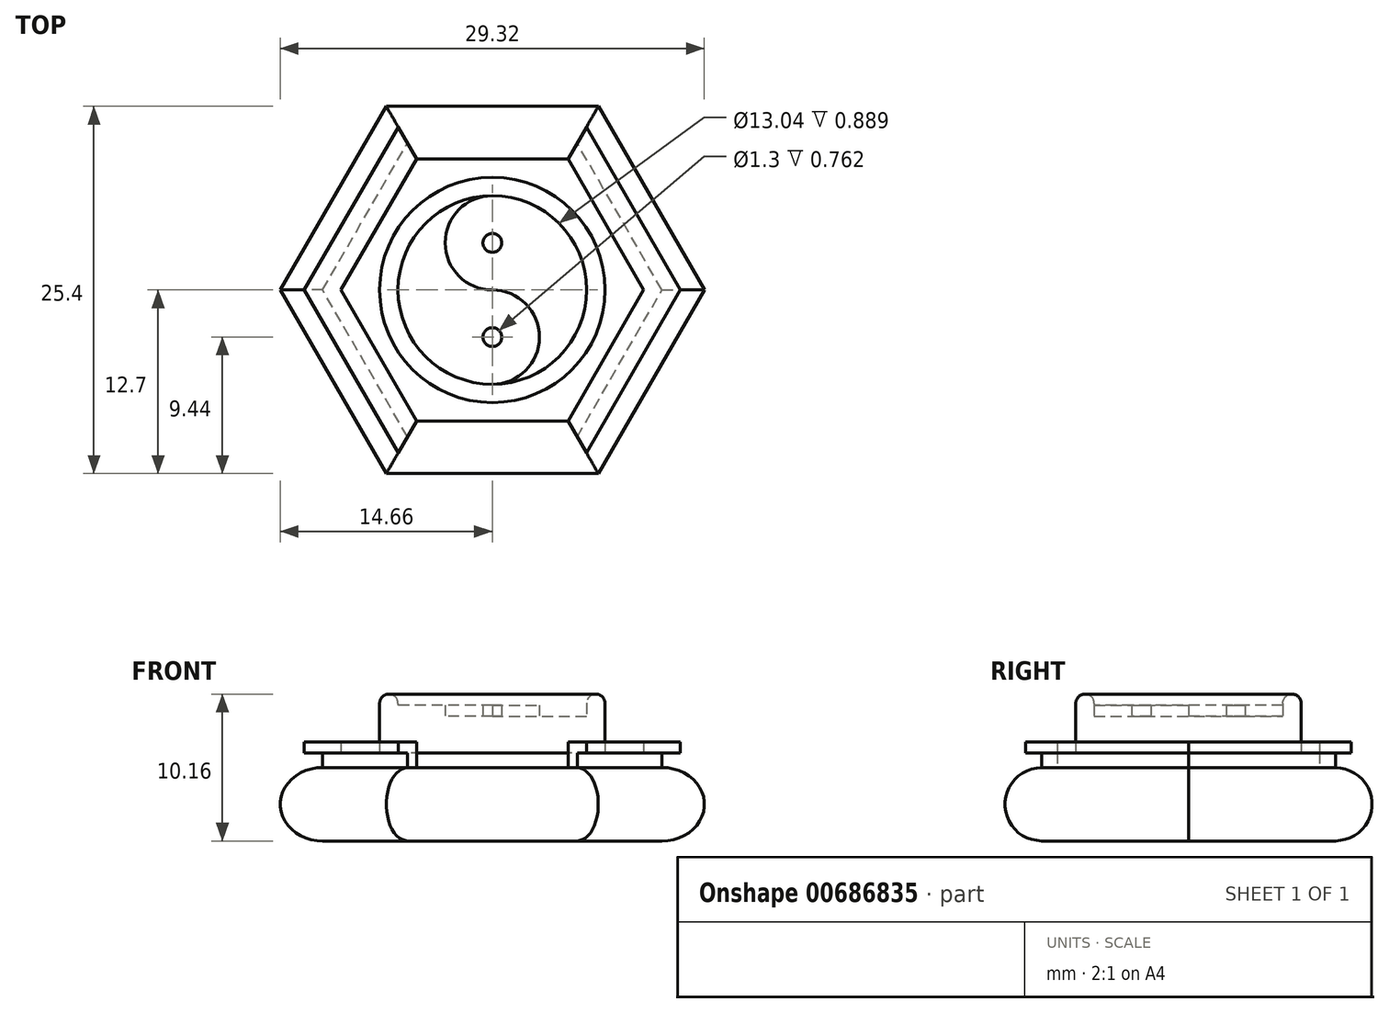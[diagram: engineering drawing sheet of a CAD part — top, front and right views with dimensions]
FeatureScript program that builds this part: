
annotation { "Feature Type Name" : "Feature", "Feature Type Description" : "" }
export const myFeature = defineFeature(function(context is Context, id is Id, definition is map)
    precondition{}
    {
        {
            var Q0;
            Q0=qCreatedBy(makeId("Front.planeOp"),FACE);
            var sketch = newSketch(context, id + "F0", { "sketchPlane" : qUnion([Q0])});
            skLineSegment(sketch, "E0", {"start": v(0, 0) * mm, "end": v(-12.7, 0) * mm});
            skLineSegment(sketch, "E1", {"start": v(-12.7, 0) * mm, "end": v(-12.7, 5.08) * mm, "construction": true});
            skLineSegment(sketch, "E2", {"start": v(12.7, 5.08) * mm, "end": v(12.7, 0) * mm, "construction": true});
            skLineSegment(sketch, "E3", {"start": v(12.7, 0) * mm, "end": v(0, 0) * mm});
            skArc(sketch, "E4", {"start": v(12.7, 0) * mm, "mid": v(15.24, 2.54) * mm, "end": v(12.7, 5.08) * mm});
            skArc(sketch, "E5", {"start": v(-12.7, 5.08) * mm, "mid": v(-15.24, 2.54) * mm, "end": v(-12.7, 0) * mm});
            skLineSegment(sketch, "E6", {"start": v(0, 0) * mm, "end": v(0, 5.08) * mm, "construction": true});
            skLineSegment(sketch, "E7", {"start": v(12.7, 2.54) * mm, "end": v(15.24, 2.54) * mm, "construction": true});
            skLineSegment(sketch, "E8", {"start": v(-12.7, 5.08) * mm, "end": v(12.7, 5.08) * mm});
            skPoint(sketch, "E9", {"position": v(0, 5.08) * mm});
            skSolve(sketch);
        }
        {
            var Q0;
            Q0=qSketchRegion(id+"F0",true);
            extrude(context, id + "F1", {"entities" : qUnion([Q0]), "endBound" : BoundingType.SYMMETRIC, "depth" : 25.4 * mm, "offsetDistance" : 25.4 * mm});
        }
        {
            var Q0;
            Q0=qCreatedBy(makeId("Right.planeOp"),FACE);
            var sketch = newSketch(context, id + "F2", { "sketchPlane" : qUnion([Q0])});
            skLineSegment(sketch, "E10", {"start": v(0, 0) * mm, "end": v(-10.16, 0) * mm, "construction": true});
            skLineSegment(sketch, "E11", {"start": v(0, 0) * mm, "end": v(10.16, 0) * mm, "construction": true});
            skLineSegment(sketch, "E12", {"start": v(-10.16, 0) * mm, "end": v(-10.16, 5.08) * mm, "construction": true});
            skLineSegment(sketch, "E13", {"start": v(10.16, 0) * mm, "end": v(10.16, 5.08) * mm, "construction": true});
            skArc(sketch, "E14", {"start": v(10.16, 0) * mm, "mid": v(12.7, 2.54) * mm, "end": v(10.16, 5.08) * mm});
            skArc(sketch, "E15", {"start": v(-10.16, 5.08) * mm, "mid": v(-12.7, 2.54) * mm, "end": v(-10.16, 0) * mm});
            skLineSegment(sketch, "E16", {"start": v(0, 0) * mm, "end": v(0, 5.08) * mm, "construction": true});
            skLineSegment(sketch, "E17", {"start": v(29.21, 5.08) * mm, "end": v(29.21, 0) * mm});
            skLineSegment(sketch, "E18", {"start": v(-29.21, 5.08) * mm, "end": v(-29.21, 0) * mm});
            skLineSegment(sketch, "E19", {"start": v(-10.16, 0) * mm, "end": v(-29.21, 0) * mm});
            skLineSegment(sketch, "E20", {"start": v(-10.16, 2.54) * mm, "end": v(-12.7, 2.54) * mm, "construction": true});
            skLineSegment(sketch, "E21", {"start": v(29.21, 0) * mm, "end": v(10.16, 0) * mm});
            skLineSegment(sketch, "E22", {"start": v(0, 0) * mm, "end": v(0, 0) * mm});
            skLineSegment(sketch, "E23", {"start": v(10.16, 5.08) * mm, "end": v(-10.16, 5.08) * mm, "construction": true});
            skLineSegment(sketch, "E24", {"start": v(29.21, 5.08) * mm, "end": v(10.16, 5.08) * mm});
            skLineSegment(sketch, "E25", {"start": v(-29.21, 5.08) * mm, "end": v(-10.16, 5.08) * mm});
            skSolve(sketch);
        }
        {
            var Q0;
            Q0=qSketchRegion(id+"F2",true);
            extrude(context, id + "F3", {"entities" : qUnion([Q0]), "operationType" : NewBodyOperationType.REMOVE, "endBound" : BoundingType.SYMMETRIC, "depth" : 50.8 * mm, "offsetDistance" : 25.4 * mm});
        }
        {
            var Q0;
            Q0=sQuery(id+"F0.wireOp",EDGE,"E6");
            cPlane(context, id + "F4", {"entities" : qUnion([Q0]), "cplaneType" : CPlaneType.LINE_ANGLE, "offset" : 25.4 * mm, "angle" : 120 * degree, "width" : 152.4 * mm, "height" : 152.4 * mm});
        }
        {
            var Q0;
            Q0=qCreatedBy(id+"F4.planeOp",FACE);
            var sketch = newSketch(context, id + "F5", { "sketchPlane" : qUnion([Q0])});
            skLineSegment(sketch, "E26", {"start": v(0, 0) * mm, "end": v(-10.16, 0) * mm, "construction": true});
            skLineSegment(sketch, "E27", {"start": v(0, 0) * mm, "end": v(10.16, 0) * mm, "construction": true});
            skLineSegment(sketch, "E28", {"start": v(-10.16, 0) * mm, "end": v(-10.16, 5.08) * mm, "construction": true});
            skLineSegment(sketch, "E29", {"start": v(10.16, 0) * mm, "end": v(10.16, 5.08) * mm, "construction": true});
            skArc(sketch, "E30", {"start": v(10.16, 0) * mm, "mid": v(12.7, 2.54) * mm, "end": v(10.16, 5.08) * mm});
            skArc(sketch, "E31", {"start": v(-10.16, 5.08) * mm, "mid": v(-12.7, 2.54) * mm, "end": v(-10.16, 0) * mm});
            skLineSegment(sketch, "E32", {"start": v(0, 0) * mm, "end": v(0, 5.08) * mm, "construction": true});
            skLineSegment(sketch, "E33", {"start": v(29.21, 5.08) * mm, "end": v(29.21, 0) * mm});
            skLineSegment(sketch, "E34", {"start": v(-29.21, 5.08) * mm, "end": v(-29.21, 0) * mm});
            skLineSegment(sketch, "E35", {"start": v(-10.16, 0) * mm, "end": v(-29.21, 0) * mm});
            skLineSegment(sketch, "E36", {"start": v(-10.16, 2.54) * mm, "end": v(-12.7, 2.54) * mm, "construction": true});
            skLineSegment(sketch, "E37", {"start": v(29.21, 0) * mm, "end": v(10.16, 0) * mm});
            skLineSegment(sketch, "E38", {"start": v(0, 0) * mm, "end": v(0, 0) * mm});
            skLineSegment(sketch, "E39", {"start": v(10.16, 5.08) * mm, "end": v(-10.16, 5.08) * mm, "construction": true});
            skLineSegment(sketch, "E40", {"start": v(29.21, 5.08) * mm, "end": v(10.16, 5.08) * mm});
            skLineSegment(sketch, "E41", {"start": v(-29.21, 5.08) * mm, "end": v(-10.16, 5.08) * mm});
            skSolve(sketch);
        }
        {
            var Q0;
            Q0=qSketchRegion(id+"F5",true);
            var Q1;
            Q1=sQuery(id+"FHUch5MhYWofbFd_1.wireOp",EDGE,"UJUXWhbe-ns99-R938-MBjs-qnEI7qI75ZtX");
            var Q2;
            Q2=sQuery(id+"FHUch5MhYWofbFd_1.wireOp",EDGE,"TGRI2bbO-5mKc-ZYGL-RI2u-ax8UZepCr2S6");
            var Q3;
            Q3=sQuery(id+"FHUch5MhYWofbFd_1.wireOp",EDGE,"3EN97P5a-7fpQ-fkxS-kFIG-O94JdEreBvdc");
            var Q4;
            Q4=sQuery(id+"FHUch5MhYWofbFd_1.wireOp",EDGE,"BLXI86f6-p3FV-xg8e-vcjV-MuaEN1ZbEeBN");
            var Q5;
            Q5=sQuery(id+"FHUch5MhYWofbFd_1.wireOp",EDGE,"K6Pg9hkI-HhUm-eWt8-lgsy-rQcUfMNRkeRX");
            var Q6;
            Q6=sQuery(id+"FHUch5MhYWofbFd_1.wireOp",EDGE,"8MWXePed-qfWZ-9kiI-xQLn-RgFZeWpe4DeW");
            var Q7;
            Q7=sQuery(id+"FHUch5MhYWofbFd_1.wireOp",EDGE,"ujHeR1Bt-oqxH-zWrO-aF7a-1cGxx1oxEC4p");
            var Q8;
            Q8=sQuery(id+"FHUch5MhYWofbFd_1.wireOp",EDGE,"ezDig2bh-fpcZ-qdXg-hfEw-k3bdO8GFTHoY");
            var Q9;
            Q9=sQuery(id+"FHUch5MhYWofbFd_1.wireOp",EDGE,"TL3t9Hpy-tibO-WM6d-k033-ZjCVjvvUcohB");
            var Q10;
            Q10=sQuery(id+"FHUch5MhYWofbFd_1.wireOp",EDGE,"H6XLH3zd-cpDk-JRaX-qujs-Kg6a5HbhHDUq");
            var Q11;
            Q11=sQuery(id+"FHUch5MhYWofbFd_1.wireOp",EDGE,"XlrNxneH-uq2I-L97s-EfPg-StDvBexp0ezL");
            var Q12;
            Q12=sQuery(id+"FHUch5MhYWofbFd_1.wireOp",EDGE,"V9PWrxtB-5fyD-G3Op-kF2t-xwj5HEO20ic1");
            var Q13;
            Q13=sQuery(id+"FHUch5MhYWofbFd_1.wireOp",EDGE,"DBsLzJAx-6rkW-YoXi-OfuC-MLqgEexGkzpa");
            extrude(context, id + "F6", {"entities" : qUnion([Q0]), "operationType" : NewBodyOperationType.REMOVE, "surfaceEntities" : qUnion([Q1, Q2, Q3, Q4, Q5, Q6, Q7, Q8, Q9, Q10, Q11, Q12, Q13]), "endBound" : BoundingType.SYMMETRIC, "oppositeDirection" : true, "depth" : 50.8 * mm, "offsetDistance" : 25.4 * mm});
        }
        {
            var Q0;
            Q0=sQuery(id+"F0.wireOp",EDGE,"E6");
            cPlane(context, id + "F7", {"entities" : qUnion([Q0]), "cplaneType" : CPlaneType.LINE_ANGLE, "offset" : 25.4 * mm, "angle" : 60 * degree, "width" : 152.4 * mm, "height" : 152.4 * mm});
        }
        {
            var Q0;
            Q0=qCreatedBy(id+"F7.planeOp",FACE);
            var sketch = newSketch(context, id + "F8", { "sketchPlane" : qUnion([Q0])});
            skLineSegment(sketch, "E42", {"start": v(0, 0) * mm, "end": v(-10.16, 0) * mm, "construction": true});
            skLineSegment(sketch, "E43", {"start": v(0, 0) * mm, "end": v(10.16, 0) * mm, "construction": true});
            skLineSegment(sketch, "E44", {"start": v(-10.16, 0) * mm, "end": v(-10.16, 5.08) * mm, "construction": true});
            skLineSegment(sketch, "E45", {"start": v(10.16, 0) * mm, "end": v(10.16, 5.08) * mm, "construction": true});
            skArc(sketch, "E46", {"start": v(10.16, 0) * mm, "mid": v(12.7, 2.54) * mm, "end": v(10.16, 5.08) * mm});
            skArc(sketch, "E47", {"start": v(-10.16, 5.08) * mm, "mid": v(-12.7, 2.54) * mm, "end": v(-10.16, 0) * mm});
            skLineSegment(sketch, "E48", {"start": v(0, 0) * mm, "end": v(0, 5.08) * mm, "construction": true});
            skLineSegment(sketch, "E49", {"start": v(29.21, 5.08) * mm, "end": v(29.21, 0) * mm});
            skLineSegment(sketch, "E50", {"start": v(-29.21, 5.08) * mm, "end": v(-29.21, 0) * mm});
            skLineSegment(sketch, "E51", {"start": v(-10.16, 0) * mm, "end": v(-29.21, 0) * mm});
            skLineSegment(sketch, "E52", {"start": v(-10.16, 2.54) * mm, "end": v(-12.7, 2.54) * mm, "construction": true});
            skLineSegment(sketch, "E53", {"start": v(29.21, 0) * mm, "end": v(10.16, 0) * mm});
            skLineSegment(sketch, "E54", {"start": v(0, 0) * mm, "end": v(0, 0) * mm});
            skLineSegment(sketch, "E55", {"start": v(10.16, 5.08) * mm, "end": v(-10.16, 5.08) * mm, "construction": true});
            skLineSegment(sketch, "E56", {"start": v(29.21, 5.08) * mm, "end": v(10.16, 5.08) * mm});
            skLineSegment(sketch, "E57", {"start": v(-29.21, 5.08) * mm, "end": v(-10.16, 5.08) * mm});
            skSolve(sketch);
        }
        {
            var Q0;
            Q0=qSketchRegion(id+"F8",true);
            extrude(context, id + "F9", {"entities" : qUnion([Q0]), "operationType" : NewBodyOperationType.REMOVE, "endBound" : BoundingType.SYMMETRIC, "oppositeDirection" : true, "depth" : 50.8 * mm, "offsetDistance" : 25.4 * mm});
        }
        {
            var Q0;
            Q0=makeQuery(id+"FriaykctB5W3C7Q_1.boolean.opBoolean","SPLIT",FACE,{"disambiguationData":[TD([makeQuery(id+"F6.boolean.opBoolean","COPY",FACE,{"derivedFrom":makeQuery(id+"F6.opExtrude","SWEPT_FACE",FACE,{"disambiguationData":[OSD([sQuery(id+"F5.wireOp",EDGE,"E30")])]})})])],"derivedFrom":makeQuery(id+"F1.opExtrude","SWEPT_FACE",FACE,{"disambiguationData":[OSD([sQuery(id+"F0.wireOp",EDGE,"E8")])]})});
            var sketch = newSketch(context, id + "F10", { "sketchPlane" : qUnion([Q0])});
            skLineSegment(sketch, "E58", {"start": v(5.87, 10.16) * mm, "end": v(6.5, 11.26) * mm});
            skLineSegment(sketch, "E59", {"start": v(6.5, 11.26) * mm, "end": v(13, 0) * mm});
            skLineSegment(sketch, "E60", {"start": v(13, 0) * mm, "end": v(6.5, -11.26) * mm});
            skLineSegment(sketch, "E61", {"start": v(-5.87, 10.16) * mm, "end": v(-6.5, 11.26) * mm});
            skLineSegment(sketch, "E62", {"start": v(-6.5, 11.26) * mm, "end": v(-13, 0) * mm});
            skLineSegment(sketch, "E63", {"start": v(-13, 0) * mm, "end": v(-6.5, -11.26) * mm});
            skLineSegment(sketch, "E64", {"start": v(-6.5, -11.26) * mm, "end": v(-5.87, -10.16) * mm});
            skLineSegment(sketch, "E65", {"start": v(6.5, -11.26) * mm, "end": v(5.87, -10.16) * mm});
            skLineSegment(sketch, "E66", {"start": v(5.23, 9.06) * mm, "end": v(10.46, 0) * mm});
            skLineSegment(sketch, "E67", {"start": v(10.46, 0) * mm, "end": v(5.23, -9.06) * mm});
            skLineSegment(sketch, "E68", {"start": v(5.23, -9.06) * mm, "end": v(5.87, -10.16) * mm});
            skLineSegment(sketch, "E69", {"start": v(0, 0) * mm, "end": v(5.23, 9.06) * mm, "construction": true});
            skLineSegment(sketch, "E70", {"start": v(5.23, 9.06) * mm, "end": v(5.87, 10.16) * mm});
            skLineSegment(sketch, "E71", {"start": v(0, 0) * mm, "end": v(-5.23, 9.06) * mm, "construction": true});
            skLineSegment(sketch, "E72", {"start": v(-5.23, 9.06) * mm, "end": v(-5.87, 10.16) * mm});
            skLineSegment(sketch, "E73", {"start": v(-5.23, 9.06) * mm, "end": v(-10.46, 0) * mm});
            skLineSegment(sketch, "E74", {"start": v(-10.46, 0) * mm, "end": v(-5.23, -9.06) * mm});
            skLineSegment(sketch, "E75", {"start": v(-5.23, -9.06) * mm, "end": v(-5.87, -10.16) * mm});
            skLineSegment(sketch, "E76", {"start": v(-5.23, -9.06) * mm, "end": v(5.23, -9.06) * mm});
            skLineSegment(sketch, "E77", {"start": v(-5.23, 9.06) * mm, "end": v(5.23, 9.06) * mm});
            skSolve(sketch);
        }
        {
            var Q0;
            Q0=makeQuery(id+"F10.imprint","IMPRINT",FACE,{"disambiguationData":[TD([[makeQuery(id+"F10.imprint","IMPRINT",EDGE,{"derivedFrom":sQuery(id+"F10.wireOp",EDGE,"E72")}),1.0]])]});
            var Q1;
            Q1=makeQuery(id+"F10.imprint","IMPRINT",FACE,{"disambiguationData":[TD([[makeQuery(id+"F10.imprint","IMPRINT",EDGE,{"derivedFrom":sQuery(id+"F10.wireOp",EDGE,"E61")}),1.0]])]});
            var Q2;
            Q2=makeQuery(id+"F10.imprint","IMPRINT",FACE,{"disambiguationData":[TD([[makeQuery(id+"F10.imprint","IMPRINT",EDGE,{"derivedFrom":sQuery(id+"F10.wireOp",EDGE,"E66")}),1.0]])]});
            var Q3;
            Q3=makeQuery(id+"F10.imprint","IMPRINT",FACE,{"disambiguationData":[TD([[makeQuery(id+"F10.imprint","IMPRINT",EDGE,{"derivedFrom":sQuery(id+"F10.wireOp",EDGE,"E58")}),-1.0]])]});
            extrude(context, id + "F11", {"entities" : qUnion([Q0, Q1, Q2, Q3]), "operationType" : NewBodyOperationType.ADD, "depth" : 1.78 * mm, "offsetDistance" : 25.4 * mm});
        }
        {
            var Q0;
            Q0=makeQuery(id+"F10.imprint","IMPRINT",FACE,{"disambiguationData":[TD([[makeQuery(id+"F10.imprint","IMPRINT",EDGE,{"derivedFrom":sQuery(id+"F10.wireOp",EDGE,"E58")}),-1.0]])]});
            var Q1;
            Q1=makeQuery(id+"F10.imprint","IMPRINT",FACE,{"disambiguationData":[TD([[makeQuery(id+"F10.imprint","IMPRINT",EDGE,{"derivedFrom":sQuery(id+"F10.wireOp",EDGE,"E61")}),1.0]])]});
            extrude(context, id + "F12", {"entities" : qUnion([Q0, Q1]), "operationType" : NewBodyOperationType.REMOVE, "depth" : 1.02 * mm, "offsetDistance" : 25.4 * mm});
        }
        {
            var Q0;
            Q0=makeQuery(id+"F10.imprint","IMPRINT",FACE,{"disambiguationData":[TD([[makeQuery(id+"F10.imprint","IMPRINT",EDGE,{"derivedFrom":sQuery(id+"F10.wireOp",EDGE,"E66")}),-1.0]])]});
            extrude(context, id + "F13", {"entities" : qUnion([Q0]), "operationType" : NewBodyOperationType.ADD, "depth" : 1.02 * mm, "offsetDistance" : 25.4 * mm});
        }
        {
            var Q0;
            Q0=makeQuery(id+"F13.opExtrude","CAP_FACE",FACE,{"disambiguationData":[OSD([sQuery(id+"F10.wireOp",EDGE,"E66"),sQuery(id+"F10.wireOp",EDGE,"E67"),sQuery(id+"F10.wireOp",EDGE,"E73"),sQuery(id+"F10.wireOp",EDGE,"E74"),sQuery(id+"F10.wireOp",EDGE,"E76"),sQuery(id+"F10.wireOp",EDGE,"E77")])],"isStart":false});
            var sketch = newSketch(context, id + "F14", { "sketchPlane" : qUnion([Q0])});
            skLineSegment(sketch, "E78", {"start": v(-5.23, 9.06) * mm, "end": v(5.23, 9.06) * mm, "construction": true});
            skLineSegment(sketch, "E79", {"start": v(5.23, 9.06) * mm, "end": v(10.46, 0) * mm, "construction": true});
            skLineSegment(sketch, "E80", {"start": v(10.46, 0) * mm, "end": v(5.23, -9.06) * mm, "construction": true});
            skLineSegment(sketch, "E81", {"start": v(5.23, -9.06) * mm, "end": v(-5.23, -9.06) * mm, "construction": true});
            skLineSegment(sketch, "E82", {"start": v(-5.23, -9.06) * mm, "end": v(-10.46, 0) * mm, "construction": true});
            skLineSegment(sketch, "E83", {"start": v(-10.46, 0) * mm, "end": v(-5.23, 9.06) * mm, "construction": true});
            skLineSegment(sketch, "E84", {"start": v(-6.29, -7.23) * mm, "end": v(-6.29, 7.23) * mm, "construction": true});
            skLineSegment(sketch, "E85", {"start": v(0, 9.06) * mm, "end": v(0, 6.52) * mm, "construction": true});
            skLineSegment(sketch, "E86", {"start": v(0, 6.52) * mm, "end": v(0, 3.91) * mm, "construction": true});
            skLineSegment(sketch, "E87", {"start": v(0, 3.91) * mm, "end": v(0, 2.6) * mm, "construction": true});
            skLineSegment(sketch, "E88", {"start": v(0, 2.6) * mm, "end": v(0, 0) * mm, "construction": true});
            skLineSegment(sketch, "E89", {"start": v(0, 0) * mm, "end": v(0, -2.6) * mm, "construction": true});
            skLineSegment(sketch, "E90", {"start": v(0, -3.91) * mm, "end": v(0, -6.52) * mm, "construction": true});
            skLineSegment(sketch, "E91", {"start": v(-5.65, 3.26) * mm, "end": v(-0.65, 3.26) * mm, "construction": true});
            skPoint(sketch, "E91.endSnap0", {"position": v(0, 3.26) * mm});
            skLineSegment(sketch, "E92", {"start": v(0.65, 3.26) * mm, "end": v(5.65, 3.26) * mm, "construction": true});
            skLineSegment(sketch, "E93", {"start": v(0, 3.26) * mm, "end": v(0, 3.26) * mm});
            skLineSegment(sketch, "E94", {"start": v(-5.65, -3.26) * mm, "end": v(-0.65, -3.26) * mm, "construction": true});
            skLineSegment(sketch, "E95", {"start": v(0.65, -3.26) * mm, "end": v(5.65, -3.26) * mm, "construction": true});
            skLineSegment(sketch, "E96", {"start": v(-0.65, 3.26) * mm, "end": v(0, 3.26) * mm, "construction": true});
            skLineSegment(sketch, "E97", {"start": v(0.65, 3.26) * mm, "end": v(0, 3.26) * mm, "construction": true});
            skLineSegment(sketch, "E98", {"start": v(0, -2.6) * mm, "end": v(0, -3.91) * mm, "construction": true});
            skLineSegment(sketch, "E99", {"start": v(-0.65, -3.26) * mm, "end": v(0, -3.26) * mm, "construction": true});
            skLineSegment(sketch, "E100", {"start": v(0, -3.26) * mm, "end": v(0.65, -3.26) * mm, "construction": true});
            skCircle(sketch, "E101", {"center": v(0, 0) * mm, "radius": 6.52 * mm});
            skCircle(sketch, "E102", {"center": v(0, 3.26) * mm, "radius": 3.26 * mm});
            skCircle(sketch, "E103", {"center": v(0, -3.26) * mm, "radius": 3.26 * mm});
            skCircle(sketch, "E104", {"center": v(0, 3.26) * mm, "radius": 0.65 * mm});
            skCircle(sketch, "E105", {"center": v(0, -3.26) * mm, "radius": 0.65 * mm});
            skLineSegment(sketch, "E106", {"start": v(-4.28, 9.06) * mm, "end": v(-4.28, -9.06) * mm, "construction": true});
            skLineSegment(sketch, "E107", {"start": v(0, 6.52) * mm, "end": v(0, 9.06) * mm, "construction": true});
            skCircle(sketch, "E108", {"center": v(0, 0) * mm, "radius": 7.8 * mm});
            skLineSegment(sketch, "E109", {"start": v(-7.8, 0) * mm, "end": v(-6.52, 0) * mm, "construction": true});
            skSolve(sketch);
        }
        {
            var Q0;
            {var subQ0=sQuery(id+"F14.wireOp",EDGE,"E102");var subQ1=sQuery(id+"F14.wireOp",EDGE,"E101");var subQ2=makeQuery(id+"F14.imprint","INTERSECT",VERTEX,{"derivedFrom":[subQ1,subQ0]});Q0=makeQuery(id+"F14.imprint","IMPRINT",FACE,{"disambiguationData":[TD([[makeQuery(id+"F14.imprint","IMPRINT",EDGE,{"disambiguationData":[TD([[subQ2,-1.0]])],"derivedFrom":subQ1}),1.0]])]});}
            var Q1;
            Q1=makeQuery(id+"F14.imprint","IMPRINT",FACE,{"disambiguationData":[TD([[makeQuery(id+"F14.imprint","IMPRINT",EDGE,{"derivedFrom":sQuery(id+"F14.wireOp",EDGE,"E105")}),-1.0]])]});
            var Q2;
            Q2=makeQuery(id+"F14.imprint","IMPRINT",FACE,{"disambiguationData":[TD([[makeQuery(id+"F14.imprint","IMPRINT",EDGE,{"derivedFrom":sQuery(id+"F14.wireOp",EDGE,"E104")}),1.0]])]});
            extrude(context, id + "F15", {"entities" : qUnion([Q0, Q1, Q2]), "operationType" : NewBodyOperationType.ADD, "depth" : 3.3 * mm, "offsetDistance" : 25.4 * mm});
        }
        {
            var Q0;
            {var subQ0=sQuery(id+"F14.wireOp",EDGE,"E102");var subQ1=sQuery(id+"F14.wireOp",EDGE,"E101");var subQ2=makeQuery(id+"F14.imprint","INTERSECT",VERTEX,{"derivedFrom":[subQ1,subQ0]});Q0=makeQuery(id+"F14.imprint","IMPRINT",FACE,{"disambiguationData":[TD([[makeQuery(id+"F14.imprint","IMPRINT",EDGE,{"disambiguationData":[TD([[subQ2,1.0]])],"derivedFrom":subQ1}),1.0]])]});}
            var Q1;
            Q1=makeQuery(id+"F14.imprint","IMPRINT",FACE,{"disambiguationData":[TD([[makeQuery(id+"F14.imprint","IMPRINT",EDGE,{"derivedFrom":sQuery(id+"F14.wireOp",EDGE,"E105")}),1.0]])]});
            var Q2;
            Q2=makeQuery(id+"F14.imprint","IMPRINT",FACE,{"disambiguationData":[TD([[makeQuery(id+"F14.imprint","IMPRINT",EDGE,{"derivedFrom":sQuery(id+"F14.wireOp",EDGE,"E104")}),-1.0]])]});
            extrude(context, id + "F16", {"entities" : qUnion([Q0, Q1, Q2]), "operationType" : NewBodyOperationType.ADD, "depth" : 2.54 * mm, "offsetDistance" : 25.4 * mm});
        }
        {
            var Q0;
            Q0=makeQuery(id+"F14.imprint","IMPRINT",FACE,{"disambiguationData":[TD([[makeQuery(id+"F14.imprint","IMPRINT",EDGE,{"derivedFrom":sQuery(id+"F14.wireOp",EDGE,"E108")}),1.0]])]});
            extrude(context, id + "F17", {"entities" : qUnion([Q0]), "operationType" : NewBodyOperationType.ADD, "depth" : 4.06 * mm, "offsetDistance" : 25.4 * mm});
        }
        {
            var Q0;
            Q0=makeQuery(id+"F17.opExtrude","CAP_EDGE",EDGE,{"disambiguationData":[OSD([sQuery(id+"F14.wireOp",EDGE,"E108")])],"isStart":false});
            var Q1;
            Q1=makeQuery(id+"F17.opExtrude","CAP_EDGE",EDGE,{"disambiguationData":[OSD([sQuery(id+"F14.wireOp",EDGE,"E101")])],"isStart":false});
            fillet(context, id + "F18", {"entities" : qUnion([Q0, Q1]), "radius" : 0.64 * mm, "tangentPropagation" : true, "allowEdgeOverflow" : false});
        }
    });
